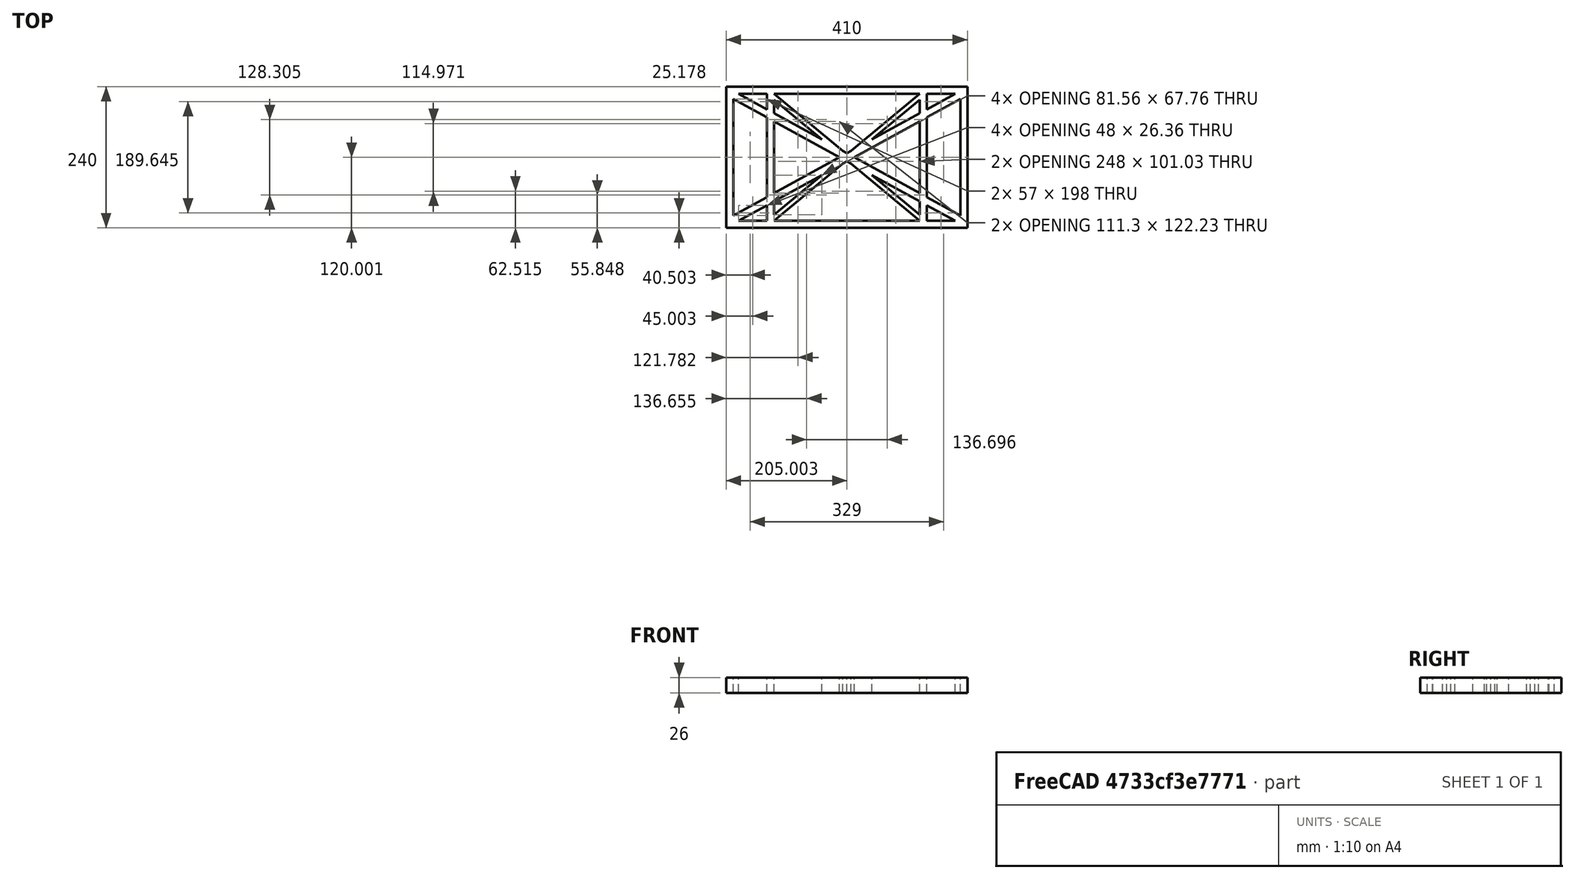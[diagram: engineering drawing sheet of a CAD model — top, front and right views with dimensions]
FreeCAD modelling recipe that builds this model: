
FCSTD DOCUMENT  (FreeCAD 0.19R0.19.2)
Label: laptopStand028
License: All rights reserved
LicenseURL: http://en.wikipedia.org/wiki/All_rights_reserved
objects: Sketcher::SketchObject×3, Part::Extrusion×1
note: 4 computed .brp shape members not serialized (recipe doc carries the construction recipe); baked Part::Feature solids carry a one-line shape summary decoded from their .brp

FEATURE [Sketcher::SketchObject] Sketch
  FullyConstrained = true
  sketch-geometry (52):
    g0: LineSegment StartX=-22.9272 StartY=136.221 StartZ=0 EndX=-22.9272 EndY=-103.779 EndZ=0
    g1: LineSegment StartX=-22.9272 StartY=136.221 StartZ=0 EndX=387.073 EndY=136.221 EndZ=0
    g2: LineSegment StartX=-22.9272 StartY=-103.779 StartZ=0 EndX=387.073 EndY=-103.779 EndZ=0
    g3: LineSegment StartX=387.073 StartY=136.221 StartZ=0 EndX=387.073 EndY=-103.779 EndZ=0
    g4: LineSegment StartX=375.073 StartY=115.221 StartZ=0 EndX=318.073 EndY=83.9235 EndZ=0
    g5: LineSegment StartX=-10.9272 StartY=-82.7794 StartZ=0 EndX=46.0728 EndY=-51.4823 EndZ=0
    g6: LineSegment StartX=-1.92719 StartY=124.221 StartZ=0 EndX=46.0728 EndY=97.8651 EndZ=0
    g7: LineSegment StartX=366.073 StartY=-91.7794 StartZ=0 EndX=318.073 EndY=-65.424 EndZ=0
    g8: LineSegment StartX=-10.9272 StartY=115.221 StartZ=0 EndX=-10.9272 EndY=-82.7794 EndZ=0
    g9: LineSegment StartX=375.073 StartY=-82.7794 StartZ=0 EndX=375.073 EndY=115.221 EndZ=0
    g10: LineSegment StartX=-1.92719 StartY=-91.7794 StartZ=0 EndX=46.0728 EndY=-91.7794 EndZ=0
    g11: LineSegment StartX=318.073 StartY=124.221 StartZ=0 EndX=366.073 EndY=124.221 EndZ=0
    g12: LineSegment StartX=306.073 StartY=-81.8102 StartZ=0 EndX=224.513 EndY=-14.0532 EndZ=0
    g13: LineSegment StartX=58.0728 StartY=114.251 StartZ=0 EndX=139.632 EndY=46.4944 EndZ=0
    g14: LineSegment StartX=306.073 StartY=124.221 StartZ=0 EndX=189.124 EndY=27.0628 EndZ=0
    g15: LineSegment StartX=58.0728 StartY=-91.7794 StartZ=0 EndX=175.022 EndY=5.37834 EndZ=0
    g16: LineSegment StartX=46.0728 StartY=124.221 StartZ=0 EndX=46.0728 EndY=97.8651 EndZ=0
    g17: LineSegment StartX=58.0728 StartY=-81.8102 StartZ=0 EndX=58.0728 EndY=-58.8351 EndZ=0
    g18: LineSegment StartX=318.073 StartY=124.221 StartZ=0 EndX=318.073 EndY=97.8651 EndZ=0
    g19: LineSegment StartX=306.073 StartY=114.251 StartZ=0 EndX=306.073 EndY=91.2763 EndZ=0
    g20: LineSegment StartX=182.073 StartY=23.1914 StartZ=0 EndX=189.124 EndY=27.0628 EndZ=0
    g21: LineSegment StartX=182.073 StartY=9.24976 StartZ=0 EndX=175.022 EndY=5.37834 EndZ=0
    g22: LineSegment StartX=224.513 StartY=46.4944 StartZ=0 EndX=306.073 EndY=114.251 EndZ=0
    g23: LineSegment StartX=175.022 StartY=27.0628 StartZ=0 EndX=58.0728 EndY=124.221 EndZ=0
    g24: LineSegment StartX=169.377 StartY=16.2206 StartZ=0 EndX=58.0728 EndY=77.3346 EndZ=0
    g25: LineSegment StartX=139.632 StartY=-14.0532 StartZ=0 EndX=58.0728 EndY=-81.8102 EndZ=0
    g26: LineSegment StartX=194.768 StartY=16.2206 StartZ=0 EndX=306.073 EndY=-44.8935 EndZ=0
    g27: LineSegment StartX=224.513 StartY=46.4944 StartZ=0 EndX=306.073 EndY=91.2763 EndZ=0
    g28: LineSegment StartX=175.022 StartY=27.0628 StartZ=0 EndX=182.073 EndY=23.1914 EndZ=0
    g29: LineSegment StartX=139.632 StartY=-14.0532 StartZ=0 EndX=58.0728 EndY=-58.8351 EndZ=0
    g30: LineSegment StartX=189.124 StartY=5.37834 StartZ=0 EndX=182.073 EndY=9.24976 EndZ=0
    g31: LineSegment StartX=189.124 StartY=5.37834 StartZ=0 EndX=306.073 EndY=-91.7794 EndZ=0
    g32: LineSegment StartX=306.073 StartY=77.3346 StartZ=0 EndX=306.073 EndY=-44.8935 EndZ=0
    g33: LineSegment StartX=318.073 StartY=83.9235 StartZ=0 EndX=318.073 EndY=-51.4823 EndZ=0
    g34: LineSegment StartX=318.073 StartY=97.8651 StartZ=0 EndX=366.073 EndY=124.221 EndZ=0
    g35: LineSegment StartX=306.073 StartY=77.3346 StartZ=0 EndX=194.768 EndY=16.2206 EndZ=0
    g36: LineSegment StartX=306.073 StartY=-58.8351 StartZ=0 EndX=224.513 EndY=-14.0532 EndZ=0
    g37: LineSegment StartX=306.073 StartY=-58.8351 StartZ=0 EndX=306.073 EndY=-81.8102 EndZ=0
    g38: LineSegment StartX=318.073 StartY=-51.4823 StartZ=0 EndX=375.073 EndY=-82.7794 EndZ=0
    g39: LineSegment StartX=318.073 StartY=-65.424 StartZ=0 EndX=318.073 EndY=-91.7794 EndZ=0
    g40: LineSegment StartX=306.073 StartY=124.221 StartZ=0 EndX=58.0728 EndY=124.221 EndZ=0
    g41: LineSegment StartX=318.073 StartY=-91.7794 StartZ=0 EndX=366.073 EndY=-91.7794 EndZ=0
    g42: LineSegment StartX=58.0728 StartY=-91.7794 StartZ=0 EndX=306.073 EndY=-91.7794 EndZ=0
    g43: LineSegment StartX=58.0728 StartY=-44.8935 StartZ=0 EndX=58.0728 EndY=77.3346 EndZ=0
    g44: LineSegment StartX=46.0728 StartY=-65.424 StartZ=0 EndX=-1.92719 EndY=-91.7794 EndZ=0
    g45: LineSegment StartX=46.0728 StartY=-65.424 StartZ=0 EndX=46.0728 EndY=-91.7794 EndZ=0
    g46: LineSegment StartX=58.0728 StartY=-44.8935 StartZ=0 EndX=169.377 EndY=16.2206 EndZ=0
    g47: LineSegment StartX=58.0728 StartY=91.2763 StartZ=0 EndX=58.0728 EndY=114.251 EndZ=0
    g48: LineSegment StartX=46.0728 StartY=83.9235 StartZ=0 EndX=46.0728 EndY=-51.4823 EndZ=0
    g49: LineSegment StartX=46.0728 StartY=124.221 StartZ=0 EndX=-1.92719 EndY=124.221 EndZ=0
    g50: LineSegment StartX=58.0728 StartY=91.2763 StartZ=0 EndX=139.632 EndY=46.4944 EndZ=0
    g51: LineSegment StartX=46.0728 StartY=83.9235 StartZ=0 EndX=-10.9272 EndY=115.221 EndZ=0
  constraints (102):
    c: Vertical(g0)
    c: Distance(g0) = 240
    c: Horizontal(g1)
    c: Distance(g1) = 410
    c: Coincident(g1,g0)
    c: Coincident(g2,g0)
    c: Horizontal(g2)
    c: Coincident(g3,g1)
    c: Vertical(g3)
    c: Coincident(g2,g3)
    c: Block(g1)
    c: Horizontal(g10)
    c: Horizontal(g11)
    c: PointOnObject(g35,g6)
    c: Coincident(g28,g20)
    c: Coincident(g30,g21)
    c: Tangent(g7,g24)
    c: PointOnObject(g24,g5)
    c: PointOnObject(g26,g4)
    c: Coincident(g20,g14)
    c: Tangent(g20,g27)
    c: Coincident(g50,g13)
    c: Coincident(g28,g23)
    c: Coincident(g22,g27)
    c: Coincident(g21,g15)
    c: Coincident(g29,g25)
    c: Tangent(g21,g29)
    c: Coincident(g36,g12)
    c: Coincident(g31,g30)
    c: Coincident(g22,g19)
    c: Tangent(g19,g32)
    c: Tangent(g18,g33)
    c: Coincident(g27,g19)
    c: Tangent(g27,g34)
    c: Coincident(g4,g33)
    c: Coincident(g35,g32)
    c: Tangent(g4,g35)
    c: Coincident(g37,g12)
    c: Tangent(g7,g36)
    c: Tangent(g32,g37)
    c: Coincident(g26,g32)
    c: Tangent(g26,g38)
    c: Coincident(g33,g38)
    c: Coincident(g39,g7)
    c: Tangent(g33,g39)
    c: Coincident(g25,g17)
    c: Tangent(g17,g43)
    c: Coincident(g29,g17)
    c: Tangent(g29,g44)
    c: Coincident(g45,g44)
    c: Tangent(g16,g45)
    c: Coincident(g5,g48)
    c: Coincident(g46,g43)
    c: Tangent(g5,g46)
    c: Tangent(g43,g47)
    c: Tangent(g16,g48)
    c: Coincident(g13,g47)
    c: PointOnObject(g40,g23)
    c: Tangent(g40,g49)
    c: Coincident(g6,g16)
    c: Coincident(g50,g47)
    c: Tangent(g6,g50)
    c: Coincident(g24,g43)
    c: Coincident(g51,g48)
    c: Tangent(g24,g51)
    c: Block(g23)
    c: Block(g14)
    c: Block(g20)
    c: Block(g40)
    c: Block(g18)
    c: Block(g34)
    c: Block(g4)
    c: Block(g38)
    c: Block(g9)
    c: Block(g36)
    c: Block(g37)
    c: Block(g7)
    c: Block(g39)
    c: Block(g22)
    c: Block(g31)
    c: Block(g42)
    c: Block(g21)
    c: Block(g15)
    c: Block(g29)
    c: Block(g25)
    c: Block(g45)
    c: Block(g44)
    c: Block(g5)
    c: Block(g8)
    c: Block(g51)
    c: Block(g6)
    c: Block(g16)
    c: Block(g13)
    c: Block(g47)
    c: Block(g35)
    c: Block(g32)
    c: Block(g24)
    c: Block(g46)
    c: Block(g49)
    c: Block(g11)
    c: Block(g41)
    c: Block(g10)
FEATURE [Part::Extrusion] Extrude
  Base = -> Sketch
  Dir = (0,0,1)
  DirMode = 2
  FaceMakerClass = Part::FaceMakerBullseye
  LengthFwd = 26
  LengthRev = 0
  Solid = true
  Symmetric = false
FEATURE [Sketcher::SketchObject] Sketch001
  FullyConstrained = false
  MapMode = 4
  Placement = pos=(0,0,0) rot=(0.57735,0.57735,0.57735;2.0944rad)
  Support = -> [Sketch]
  sketch-geometry (29):
    g0: LineSegment StartX=17.2232 StartY=-16.0875 StartZ=0 EndX=117.223 EndY=-16.0875 EndZ=0
    g1: LineSegment StartX=17.2232 StartY=-16.0875 StartZ=0 EndX=17.2232 EndY=-19.0875 EndZ=0
    g2: LineSegment StartX=117.223 StartY=-16.0875 StartZ=0 EndX=117.223 EndY=-19.0875 EndZ=0
    g3: BSplineCurve PolesCount=3 KnotsCount=2 Degree=2 IsPeriodic=0
    g4: LineSegment StartX=-9.4377 StartY=-200.664 StartZ=0 EndX=24.2583 EndY=-213.335 EndZ=0
    g5: LineSegment StartX=17.2232 StartY=-19.0875 StartZ=0 EndX=38.8094 EndY=-19.0875 EndZ=0
    g6: BSplineCurve PolesCount=4 KnotsCount=2 Degree=3 IsPeriodic=0
    g7: ArcOfCircle CenterX=73.122 CenterY=-32.2909 CenterZ=0 NormalX=0 NormalY=0 NormalZ=1 AngleXU=0 Radius=13 StartAngle=5.92268 EndAngle=9.06428
    g8: LineSegment StartX=85.2864 StartY=-36.8765 StartZ=0 EndX=78.9505 EndY=-53.7246 EndZ=0
    g9: LineSegment StartX=60.9577 StartY=-27.7052 StartZ=0 EndX=54.6191 EndY=-44.5532 EndZ=0
    g10: ArcOfCircle CenterX=66.7816 CenterY=-49.1439 CenterZ=0 NormalX=0 NormalY=0 NormalZ=1 AngleXU=0 Radius=13 StartAngle=2.78068 EndAngle=5.92131
    g11: ArcOfCircle CenterX=55.9263 CenterY=-78.1807 CenterZ=0 NormalX=0 NormalY=0 NormalZ=1 AngleXU=0 Radius=13 StartAngle=5.92268 EndAngle=9.06428
    g12: LineSegment StartX=68.0907 StartY=-82.7664 StartZ=0 EndX=61.7547 EndY=-99.6148 EndZ=0
    g13: ArcOfCircle CenterX=49.5884 CenterY=-95.0342 CenterZ=0 NormalX=0 NormalY=0 NormalZ=1 AngleXU=0 Radius=13 StartAngle=2.78068 EndAngle=5.92131
    g14: LineSegment StartX=43.7619 StartY=-73.595 StartZ=0 EndX=37.426 EndY=-90.4435 EndZ=0
    g15: ArcOfCircle CenterX=38.7206 CenterY=-124.067 CenterZ=0 NormalX=0 NormalY=0 NormalZ=1 AngleXU=0 Radius=13 StartAngle=5.92268 EndAngle=9.06428
    g16: LineSegment StartX=26.5562 StartY=-119.481 StartZ=0 EndX=20.2251 EndY=-136.329 EndZ=0
    g17: ArcOfCircle CenterX=32.3875 CenterY=-140.92 CenterZ=0 NormalX=0 NormalY=0 NormalZ=1 AngleXU=0 Radius=13 StartAngle=2.78068 EndAngle=5.92131
    g18: LineSegment StartX=50.885 StartY=-128.652 StartZ=0 EndX=44.549 EndY=-145.5 EndZ=0
    g19: ArcOfCircle CenterX=21.4715 CenterY=-169.934 CenterZ=0 NormalX=0 NormalY=0 NormalZ=1 AngleXU=0 Radius=13 StartAngle=5.92268 EndAngle=9.06428
    g20: LineSegment StartX=9.3071 StartY=-165.349 StartZ=0 EndX=2.97115 EndY=-182.197 EndZ=0
    g21: ArcOfCircle CenterX=15.1336 CenterY=-186.787 CenterZ=0 NormalX=0 NormalY=0 NormalZ=1 AngleXU=0 Radius=13 StartAngle=2.78068 EndAngle=5.92131
    g22: LineSegment StartX=33.6358 StartY=-174.52 StartZ=0 EndX=27.2999 EndY=-191.368 EndZ=0
    g23: LineSegment StartX=24.2583 StartY=-213.335 StartZ=0 EndX=25.4551 EndY=-210.153 EndZ=0
    g24: LineSegment StartX=-9.4377 StartY=-200.664 StartZ=0 EndX=-8.24091 EndY=-197.481 EndZ=0
    g25: LineSegment StartX=94.6577 StartY=-26.1351 StartZ=0 EndX=25.4551 EndY=-210.153 EndZ=0
    g26: LineSegment StartX=56.1962 StartY=-26.1351 StartZ=0 EndX=-8.24091 EndY=-197.481 EndZ=0
    g27: LineSegment StartX=56.1962 StartY=-26.1351 StartZ=0 EndX=49.1563 EndY=-44.8552 EndZ=0
    g28: LineSegment StartX=38.8094 StartY=-19.0875 StartZ=0 EndX=28.8094 EndY=-19.0875 EndZ=0
  constraints (62):
    c: Horizontal(g0)
    c: Distance(g0) = 100
    c: Block(g0)
    c: Coincident(g1,g0)
    c: Vertical(g1)
    c: Distance(g1) = 3
    c: Coincident(g2,g0)
    c: Vertical(g2)
    c: Distance(g2) = 3
    c: Block(g3)
    c: Coincident(g3,g2)
    c: Coincident(g5,g1)
    c: Horizontal(g5)
    c: Block(g6)
    c: Coincident(g6,g5)
    c: Block(g7)
    c: Distance(g8) = 18
    c: Coincident(g8,g7)
    c: Coincident(g9,g7)
    c: Block(g10)
    c: Coincident(g10,g9)
    c: Block(g9)
    c: Coincident(g12,g11)
    c: Coincident(g14,g11)
    c: Block(g13)
    c: Coincident(g13,g14)
    c: Block(g14)
    c: Block(g11)
    c: Block(g12)
    c: Coincident(g18,g15)
    c: Coincident(g16,g15)
    c: Block(g17)
    c: Coincident(g17,g16)
    c: Block(g16)
    c: Block(g15)
    c: Coincident(g22,g19)
    c: Coincident(g20,g19)
    c: Block(g21)
    c: Coincident(g21,g20)
    c: Block(g20)
    c: Block(g19)
    c: Distance(g22) = 18
    c: Block(g22)
    c: Block(g18)
    c: Distance(g23) = 3.4
    c: Equal(g23,g24) = 3.4
    c: Coincident(g24,g4)
    c: Coincident(g25,g3)
    c: Coincident(g25,g23)
    c: Coincident(g26,g6)
    c: Coincident(g26,g24)
    c: Block(g25)
    c: Block(g26)
    c: Block(g4)
    c: Block(g23)
    c: Block(g8)
    c: Coincident(g27,g6)
    c: Distance(g27) = 20
    c: Parallel(g27,g26)
    c: Coincident(g28,g5)
    c: Distance(g28) = 10
    c: Parallel(g28,g5)
FEATURE [Sketcher::SketchObject] Sketch002
  FullyConstrained = true
  Placement = pos=(0,0,0) rot=(-1,0,0;4.71239rad)
